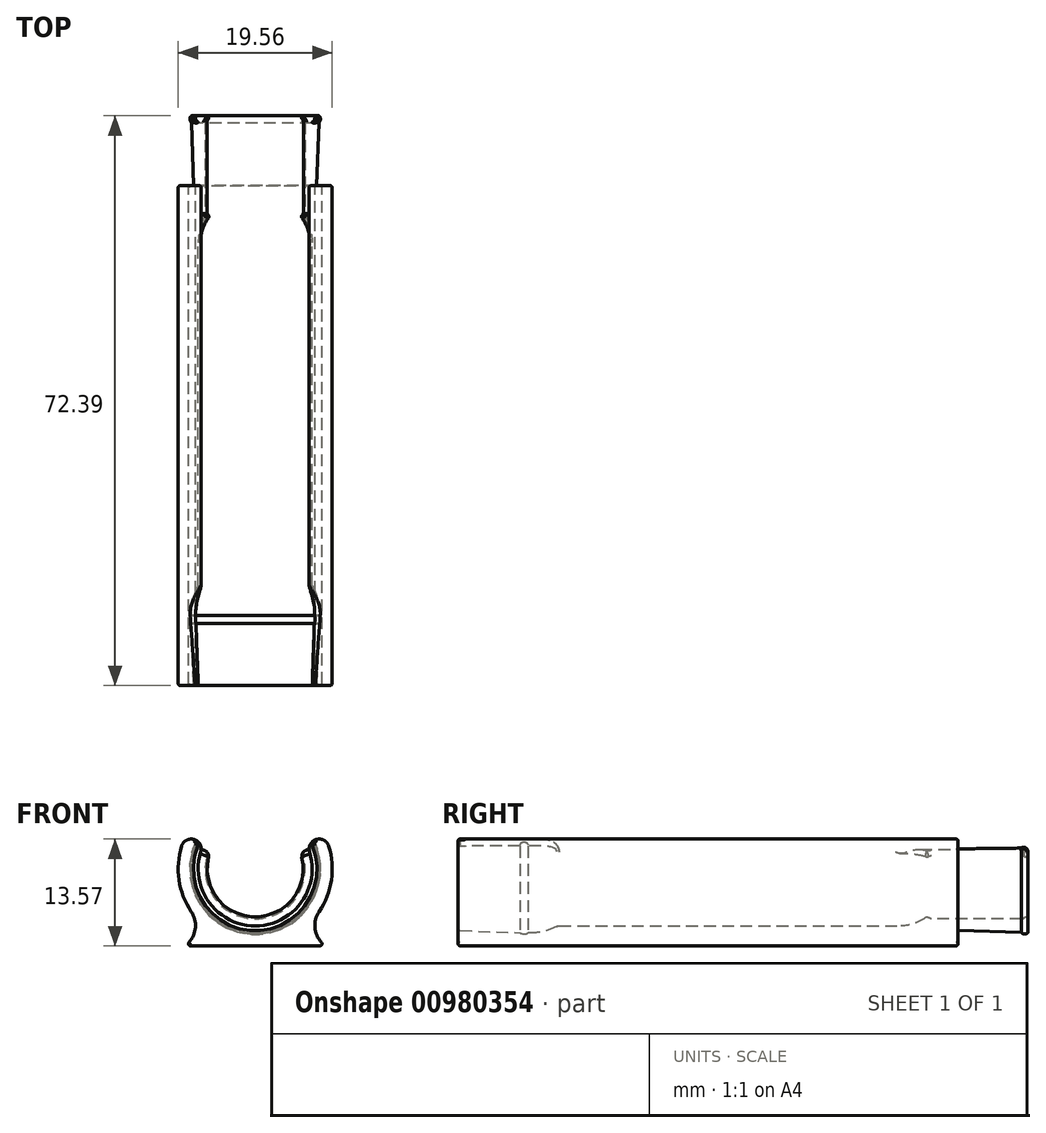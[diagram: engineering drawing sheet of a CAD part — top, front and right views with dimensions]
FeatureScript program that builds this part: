
annotation { "Feature Type Name" : "Feature", "Feature Type Description" : "" }
export const myFeature = defineFeature(function(context is Context, id is Id, definition is map)
    precondition{}
    {
        {
            var Q0;
            Q0=qCreatedBy(makeId("Front.planeOp"),FACE);
            var sketch = newSketch(context, id + "F0", { "sketchPlane" : qUnion([Q0])});
            skLineSegment(sketch, "E0", {"start": v(0, 0) * mm, "end": v(0, 2.54) * mm, "construction": true});
            skLineSegment(sketch, "E1", {"start": v(0, 0) * mm, "end": v(-8.23, 0) * mm});
            skArc(sketch, "E2", {"start": v(-6.91, 11.92) * mm, "mid": v(-5.83, 5.48) * mm, "end": v(0, 2.54) * mm});
            skArc(sketch, "E3", {"start": v(-6.91, 11.92) * mm, "mid": v(-7.75, 13.5) * mm, "end": v(-9.34, 12.67) * mm});
            skArc(sketch, "E4", {"start": v(-9.34, 12.67) * mm, "mid": v(-9.68, 8.37) * mm, "end": v(-8.12, 4.33) * mm});
            skArc(sketch, "E5", {"start": v(-8.42, 0.43) * mm, "mid": v(-7.6, 2.33) * mm, "end": v(-8.12, 4.33) * mm});
            skPoint(sketch, "E6.visualSharp", {"position": v(-8.9, 0) * mm});
            skArc(sketch, "E6.filletArc", {"start": v(-8.42, 0.43) * mm, "mid": v(-8.46, 0.15) * mm, "end": v(-8.23, 0) * mm});
            skPoint(sketch, "E7", {"position": v(-7.24, 9.78) * mm});
            skPoint(sketch, "E8", {"position": v(-6.86, 12.3) * mm});
            skArc(sketch, "E9.MirrorCS", {"start": v(6.91, 11.92) * mm, "mid": v(5.83, 5.48) * mm, "end": v(0, 2.54) * mm});
            skArc(sketch, "E10.MirrorCS", {"start": v(6.91, 11.92) * mm, "mid": v(7.75, 13.5) * mm, "end": v(9.34, 12.67) * mm});
            skArc(sketch, "E11.MirrorCS", {"start": v(9.34, 12.67) * mm, "mid": v(9.68, 8.37) * mm, "end": v(8.12, 4.33) * mm});
            skArc(sketch, "E12.MirrorCS", {"start": v(8.42, 0.43) * mm, "mid": v(7.6, 2.33) * mm, "end": v(8.12, 4.33) * mm});
            skLineSegment(sketch, "E13.MirrorCS", {"start": v(0, 0) * mm, "end": v(8.23, 0) * mm});
            skArc(sketch, "E14.MirrorCS", {"start": v(8.42, 0.43) * mm, "mid": v(8.46, 0.15) * mm, "end": v(8.23, 0) * mm});
            skSolve(sketch);
        }
        {
            var Q0;
            Q0 = qSketchRegion(id + "F0", true);
            extrude(context, id + "F1", {"entities" : qUnion([Q0]), "depth" : 63.5 * mm, "offsetDistance" : 25.4 * mm});
        }
        {
            var Q0;
            Q0=qCreatedBy(makeId("Right.planeOp"),FACE);
            var sketch = newSketch(context, id + "F2", { "sketchPlane" : qUnion([Q0])});
            skLineSegment(sketch, "E15", {"start": v(0, 9.78) * mm, "end": v(9.62, 9.78) * mm, "construction": true});
            skLineSegment(sketch, "E16", {"start": v(-4.19, 2.1) * mm, "end": v(8.02, 1.68) * mm});
            skLineSegment(sketch, "E17", {"start": v(-4.19, 2.1) * mm, "end": v(-4.19, 3.43) * mm});
            skLineSegment(sketch, "E18", {"start": v(-3.37, 3.43) * mm, "end": v(8.07, 3.43) * mm});
            skLineSegment(sketch, "E19", {"start": v(8.9, 3.43) * mm, "end": v(8.9, 1.65) * mm});
            skLineSegment(sketch, "E20", {"start": v(-68.2, 2.1) * mm, "end": v(-55.65, 1.67) * mm});
            skLineSegment(sketch, "E21", {"start": v(-68.2, 2.1) * mm, "end": v(-68.2, 3.43) * mm});
            skLineSegment(sketch, "E22", {"start": v(-68.2, 3.43) * mm, "end": v(-54.6, 3.43) * mm});
            skLineSegment(sketch, "E23", {"start": v(-54.6, 3.43) * mm, "end": v(-54.6, 1.63) * mm, "construction": true});
            skArc(sketch, "E24", {"start": v(8.9, 3.43) * mm, "mid": v(8.73, 3.67) * mm, "end": v(8.45, 3.6) * mm});
            skArc(sketch, "E25", {"start": v(-3.75, 3.6) * mm, "mid": v(-4.03, 3.67) * mm, "end": v(-4.19, 3.43) * mm});
            skPoint(sketch, "E26.visualSharp", {"position": v(-3.68, 3.43) * mm});
            skArc(sketch, "E26.filletArc", {"start": v(-3.75, 3.6) * mm, "mid": v(-3.57, 3.47) * mm, "end": v(-3.37, 3.43) * mm});
            skPoint(sketch, "E27.visualSharp", {"position": v(8.38, 3.43) * mm});
            skArc(sketch, "E27.filletArc", {"start": v(8.07, 3.43) * mm, "mid": v(8.28, 3.47) * mm, "end": v(8.45, 3.6) * mm});
            skArc(sketch, "E28", {"start": v(-54.6, 1.63) * mm, "mid": v(-51.9, 2.05) * mm, "end": v(-49.53, 3.43) * mm});
            skLineSegment(sketch, "E29", {"start": v(-54.6, 3.43) * mm, "end": v(-49.53, 3.43) * mm});
            skArc(sketch, "E30", {"start": v(8.02, 1.68) * mm, "mid": v(8.45, 1.5) * mm, "end": v(8.9, 1.65) * mm});
            skArc(sketch, "E31", {"start": v(-55.65, 1.67) * mm, "mid": v(-55.14, 1.45) * mm, "end": v(-54.6, 1.63) * mm});
            skLineSegment(sketch, "E32", {"start": v(8.02, 1.68) * mm, "end": v(8.57, 1.14) * mm, "construction": true});
            skLineSegment(sketch, "E33", {"start": v(-55.65, 1.67) * mm, "end": v(-53.42, -0.56) * mm, "construction": true});
            skLineSegment(sketch, "E34", {"start": v(-55.65, 1.67) * mm, "end": v(-54.6, 1.63) * mm});
            skLineSegment(sketch, "E35", {"start": v(8.02, 1.68) * mm, "end": v(8.9, 1.65) * mm});
            skSolve(sketch);
        }
        {
            var Q0;
            Q0=makeQuery(id+"F2.imprint","IMPRINT",FACE,{"disambiguationData":[TD([[makeQuery(id+"F2.imprint","IMPRINT",EDGE,{"derivedFrom":sQuery(id+"F2.wireOp",EDGE,"E16")}),1.0]])]});
            var Q1;
            Q1=makeQuery(id+"F2.imprint","IMPRINT",FACE,{"disambiguationData":[TD([[makeQuery(id+"F2.imprint","IMPRINT",EDGE,{"derivedFrom":sQuery(id+"F2.wireOp",EDGE,"E30")}),1.0]])]});
            var Q2;
            Q2=sQuery(id+"F2.wireOp",EDGE,"E15");
            revolve(context, id + "F3", {"operationType" : NewBodyOperationType.ADD, "surfaceOperationType" : NewSurfaceOperationType.NEW, "entities" : qUnion([Q0, Q1]), "axis" : qUnion([Q2]), "revolveType" : RevolveType.SYMMETRIC, "angle" : 220 * degree});
        }
        {
            var Q0;
            Q0=makeQuery(id+"F2.imprint","IMPRINT",FACE,{"disambiguationData":[TD([[makeQuery(id+"F2.imprint","IMPRINT",EDGE,{"derivedFrom":sQuery(id+"F2.wireOp",EDGE,"E20")}),1.0]])]});
            var Q1;
            Q1=sQuery(id+"F2.wireOp",EDGE,"E15");
            revolve(context, id + "F4", {"operationType" : NewBodyOperationType.REMOVE, "surfaceOperationType" : NewSurfaceOperationType.NEW, "entities" : qUnion([Q0]), "axis" : qUnion([Q1]), "revolveType" : RevolveType.FULL, "oppositeDirection" : true});
        }
        {
            var Q0;
            Q0=makeQuery(id+"F3.boolean.opBoolean","INTERSECT",EDGE,{"derivedFrom":[makeQuery(id+"F1.opExtrude","SWEPT_FACE",FACE,{"disambiguationData":[OSD([sQuery(id+"F0.wireOp",EDGE,"E2"),sQuery(id+"F0.wireOp",EDGE,"E9.MirrorCS")])]}),makeQuery(id+"F3.opRevolve","SWEPT_FACE",FACE,{"disambiguationData":[OSD([sQuery(id+"F2.wireOp",EDGE,"E17")])]})]});
            fillet(context, id + "F5", {"entities" : qUnion([Q0]), "radius" : 5.08 * mm, "tangentPropagation" : true, "allowEdgeOverflow" : false});
        }
        {
            var Q0;
            Q0=makeQuery(id+"F4.boolean.opBoolean","INTERSECT",EDGE,{"derivedFrom":[makeQuery(id+"F1.opExtrude","SWEPT_FACE",FACE,{"disambiguationData":[OSD([sQuery(id+"F0.wireOp",EDGE,"E3")])]}),makeQuery(id+"F4.opRevolve","SWEPT_FACE",FACE,{"disambiguationData":[OSD([sQuery(id+"F2.wireOp",EDGE,"E20")])]})]});
            var Q1;
            Q1=makeQuery(id+"F4.boolean.opBoolean","INTERSECT",EDGE,{"derivedFrom":[makeQuery(id+"F1.opExtrude","SWEPT_FACE",FACE,{"disambiguationData":[OSD([sQuery(id+"F0.wireOp",EDGE,"E10.MirrorCS")])]}),makeQuery(id+"F4.opRevolve","SWEPT_FACE",FACE,{"disambiguationData":[OSD([sQuery(id+"F2.wireOp",EDGE,"E20")])]})]});
            var Q2;
            Q2=makeQuery(id+"F3.opRevolve","CAP_EDGE",EDGE,{"disambiguationData":[OSD([sQuery(id+"F2.wireOp",EDGE,"E18")])],"isStart":false});
            var Q3;
            Q3=makeQuery(id+"F3.opRevolve","CAP_EDGE",EDGE,{"disambiguationData":[OSD([sQuery(id+"F2.wireOp",EDGE,"E18")])],"isStart":true});
            fillet(context, id + "F6", {"entities" : qUnion([Q0, Q1, Q2, Q3]), "radius" : 0.64 * mm, "tangentPropagation" : true, "allowEdgeOverflow" : false});
        }
        {
            var Q0;
            Q0=makeQuery(id+"F3.opRevolve","CAP_EDGE",EDGE,{"disambiguationData":[OSD([sQuery(id+"F2.wireOp",EDGE,"E16")])],"isStart":false});
            var Q1;
            Q1=makeQuery(id+"F3.opRevolve","CAP_EDGE",EDGE,{"disambiguationData":[OSD([sQuery(id+"F2.wireOp",EDGE,"E16")])],"isStart":true});
            fillet(context, id + "F7", {"entities" : qUnion([Q0, Q1]), "radius" : 0.46 * mm, "tangentPropagation" : true, "allowEdgeOverflow" : false});
        }
        {
            var Q0;
            Q0=makeQuery(id+"F4.boolean.opBoolean","INTERSECT",EDGE,{"derivedFrom":[makeQuery(id+"F1.opExtrude","CAP_FACE",FACE,{"disambiguationData":[OSD([sQuery(id+"F0.wireOp",EDGE,"E1"),sQuery(id+"F0.wireOp",EDGE,"E2"),sQuery(id+"F0.wireOp",EDGE,"E3"),sQuery(id+"F0.wireOp",EDGE,"E4"),sQuery(id+"F0.wireOp",EDGE,"E5"),sQuery(id+"F0.wireOp",EDGE,"E6.filletArc"),sQuery(id+"F0.wireOp",EDGE,"E9.MirrorCS"),sQuery(id+"F0.wireOp",EDGE,"E10.MirrorCS"),sQuery(id+"F0.wireOp",EDGE,"E11.MirrorCS"),sQuery(id+"F0.wireOp",EDGE,"E12.MirrorCS"),sQuery(id+"F0.wireOp",EDGE,"E13.MirrorCS"),sQuery(id+"F0.wireOp",EDGE,"E14.MirrorCS")])],"isStart":false}),makeQuery(id+"F4.opRevolve","SWEPT_FACE",FACE,{"disambiguationData":[OSD([sQuery(id+"F2.wireOp",EDGE,"E20")])]})]});
            var Q1;
            Q1=makeQuery(id+"F4.boolean.opBoolean","INTERSECT",EDGE,{"derivedFrom":[makeQuery(id+"F1.opExtrude","SWEPT_FACE",FACE,{"disambiguationData":[OSD([sQuery(id+"F0.wireOp",EDGE,"E2"),sQuery(id+"F0.wireOp",EDGE,"E9.MirrorCS")])]}),makeQuery(id+"F4.opRevolve","SWEPT_FACE",FACE,{"disambiguationData":[OSD([sQuery(id+"F2.wireOp",EDGE,"E23")])]})]});
            var Q2;
            Q2=makeQuery(id+"F3.opRevolve","SWEPT_EDGE",EDGE,{"disambiguationData":[OSD([sQuery(id+"F2.wireOp",EDGE,"E18"),sQuery(id+"F2.wireOp",EDGE,"E19")])]});
            var Q3;
            Q3=makeQuery(id+"F1.opExtrude","CAP_EDGE",EDGE,{"disambiguationData":[OSD([sQuery(id+"F0.wireOp",EDGE,"E4")])],"isStart":true});
            var Q4;
            Q4=makeQuery(id+"F3.boolean.opBoolean","INTERSECT",EDGE,{"derivedFrom":[makeQuery(id+"F1.opExtrude","SWEPT_FACE",FACE,{"disambiguationData":[OSD([sQuery(id+"F0.wireOp",EDGE,"E2"),sQuery(id+"F0.wireOp",EDGE,"E9.MirrorCS")])]}),makeQuery(id+"F3.opRevolve","SWEPT_FACE",FACE,{"disambiguationData":[OSD([sQuery(id+"F2.wireOp",EDGE,"E17")])]})]});
            var Q5;
            Q5=makeQuery(id+"FH2piJS7uuTGJ2u_1.opExtrude","CAP_EDGE",EDGE,{"disambiguationData":[OSD([sQuery(id+"FoCLsh66cKFiKgl_1.wireOp",EDGE,"11dVqFUu-e9aY-AeWq-O7nq-crDflKvgFnvz.left")])],"isStart":true});
            var Q6;
            Q6=makeQuery(id+"FH2piJS7uuTGJ2u_1.opExtrude","CAP_EDGE",EDGE,{"disambiguationData":[OSD([sQuery(id+"FoCLsh66cKFiKgl_1.wireOp",EDGE,"11dVqFUu-e9aY-AeWq-O7nq-crDflKvgFnvz.right")])],"isStart":true});
            var Q7;
            Q7=makeQuery(id+"FH2piJS7uuTGJ2u_1.opExtrude","CAP_EDGE",EDGE,{"disambiguationData":[OSD([sQuery(id+"FoCLsh66cKFiKgl_1.wireOp",EDGE,"11dVqFUu-e9aY-AeWq-O7nq-crDflKvgFnvz.top")])],"isStart":true});
            var Q8;
            Q8=makeQuery(id+"FRpYH6i3VNikOXj_1.boolean.opBoolean","COPY",EDGE,{"derivedFrom":makeQuery(id+"FRpYH6i3VNikOXj_1.opExtrude","CAP_EDGE",EDGE,{"disambiguationData":[OSD([sQuery(id+"FoCLsh66cKFiKgl_1.wireOp",EDGE,"htWPkWeC-bwWN-7SjK-EXkN-T3KBYyp8dpbN.right")])],"isStart":true})});
            var Q9;
            Q9=makeQuery(id+"FRpYH6i3VNikOXj_1.boolean.opBoolean","COPY",EDGE,{"derivedFrom":makeQuery(id+"FRpYH6i3VNikOXj_1.opExtrude","CAP_EDGE",EDGE,{"disambiguationData":[OSD([sQuery(id+"FoCLsh66cKFiKgl_1.wireOp",EDGE,"htWPkWeC-bwWN-7SjK-EXkN-T3KBYyp8dpbN.top")])],"isStart":true})});
            var Q10;
            Q10=makeQuery(id+"FRpYH6i3VNikOXj_1.boolean.opBoolean","COPY",EDGE,{"derivedFrom":makeQuery(id+"FRpYH6i3VNikOXj_1.opExtrude","CAP_EDGE",EDGE,{"disambiguationData":[OSD([sQuery(id+"FoCLsh66cKFiKgl_1.wireOp",EDGE,"htWPkWeC-bwWN-7SjK-EXkN-T3KBYyp8dpbN.left")])],"isStart":true})});
            fillet(context, id + "F8", {"entities" : qUnion([Q0, Q1, Q2, Q3, Q4, Q5, Q6, Q7, Q8, Q9, Q10]), "radius" : 0.25 * mm, "tangentPropagation" : true, "allowEdgeOverflow" : false});
        }
        {
            var Q0;
            Q0=makeQuery(id+"F2.imprint","IMPRINT",FACE,{"disambiguationData":[TD([[makeQuery(id+"F2.imprint","IMPRINT",EDGE,{"derivedFrom":sQuery(id+"F2.wireOp",EDGE,"E31")}),1.0]])]});
            var Q1;
            Q1=sQuery(id+"F2.wireOp",EDGE,"E15");
            revolve(context, id + "F9", {"operationType" : NewBodyOperationType.REMOVE, "surfaceOperationType" : NewSurfaceOperationType.NEW, "entities" : qUnion([Q0]), "axis" : qUnion([Q1]), "revolveType" : RevolveType.FULL, "oppositeDirection" : true});
        }
        {
            var Q0;
            Q0=makeQuery(id+"F3.opRevolve","SWEPT_EDGE",EDGE,{"disambiguationData":[OSD([sQuery(id+"F2.wireOp",EDGE,"E19"),sQuery(id+"F2.wireOp",EDGE,"E30"),sQuery(id+"F2.wireOp",EDGE,"E35")])]});
            var Q1;
            Q1=makeQuery(id+"F9.boolean.opBoolean","COPY",EDGE,{"derivedFrom":makeQuery(id+"F9.opRevolve","SWEPT_EDGE",EDGE,{"disambiguationData":[OSD([sQuery(id+"F2.wireOp",EDGE,"E20"),sQuery(id+"F2.wireOp",EDGE,"E31"),sQuery(id+"F2.wireOp",EDGE,"E34")])]})});
            fillet(context, id + "F10", {"entities" : qUnion([Q0, Q1]), "radius" : 0.25 * mm, "tangentPropagation" : true, "allowEdgeOverflow" : false});
        }
    });
